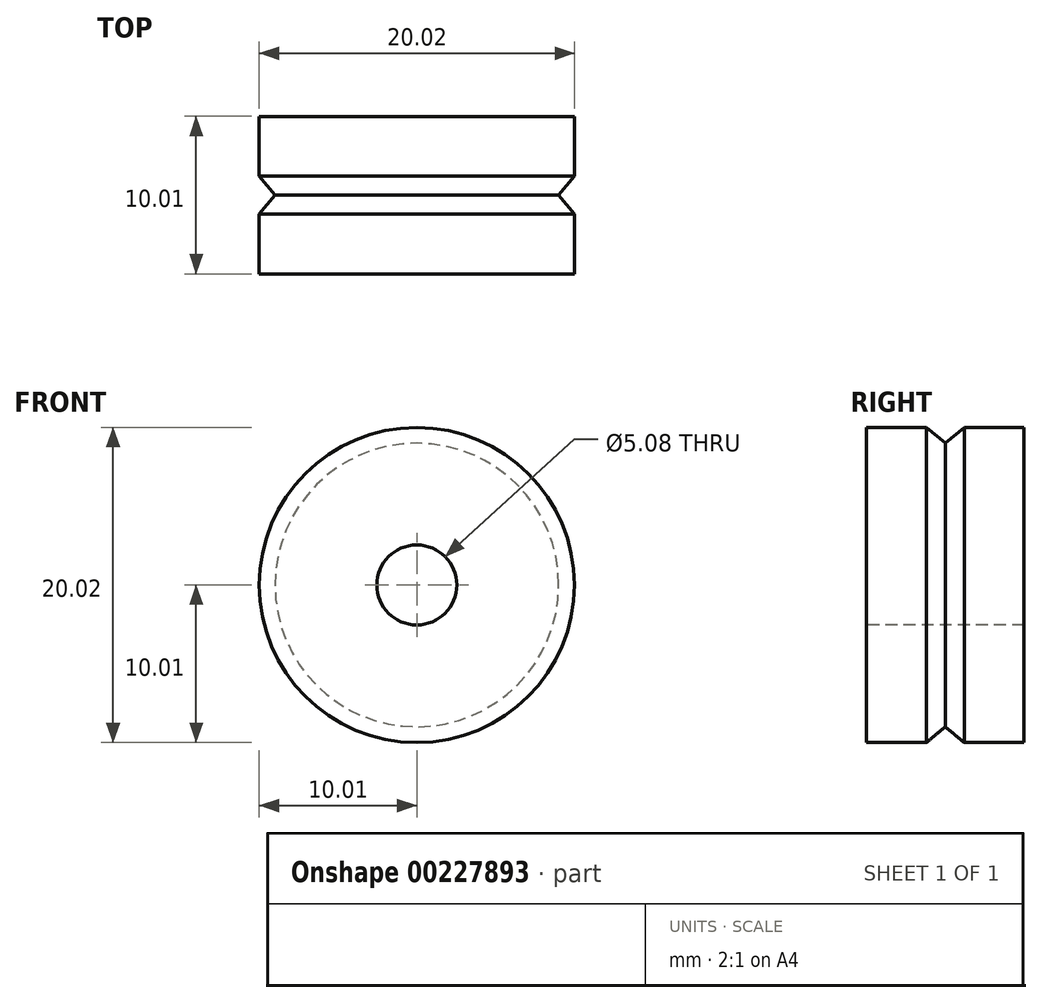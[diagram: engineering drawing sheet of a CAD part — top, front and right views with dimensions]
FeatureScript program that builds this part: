
annotation { "Feature Type Name" : "Feature", "Feature Type Description" : "" }
export const myFeature = defineFeature(function(context is Context, id is Id, definition is map)
    precondition{}
    {
        {
            var Q0;
            Q0=qCreatedBy(makeId("Right.planeOp"),FACE);
            var sketch = newSketch(context, id + "F0", { "sketchPlane" : qUnion([Q0])});
            skLineSegment(sketch, "E0", {"start": v(0, 10) * mm, "end": v(3.8, 10) * mm});
            skLineSegment(sketch, "E1", {"start": v(3.8, 10) * mm, "end": v(5, 9) * mm});
            skLineSegment(sketch, "E2", {"start": v(5, 9) * mm, "end": v(6.2, 10) * mm});
            skLineSegment(sketch, "E3", {"start": v(6.2, 10) * mm, "end": v(10, 10) * mm});
            skLineSegment(sketch, "E4", {"start": v(10, 10) * mm, "end": v(10, 0) * mm});
            skLineSegment(sketch, "E5", {"start": v(0, 0) * mm, "end": v(10, 0) * mm});
            skLineSegment(sketch, "E6", {"start": v(0, 10) * mm, "end": v(0, 0) * mm});
            skSolve(sketch);
        }
        {
            var Q0;
            Q0 = qSketchRegion(id + "F0", true);
            var Q1;
            Q1=sQuery(id+"F0.wireOp",EDGE,"E5");
            revolve(context, id + "F1", {"entities" : qUnion([Q0]), "axis" : qUnion([Q1]), "revolveType" : RevolveType.FULL});
        }
        {
            var Q0;
            Q0=makeQuery(id+"F1.opRevolve","SWEPT_FACE",FACE,{"disambiguationData":[OSD([sQuery(id+"F0.wireOp",EDGE,"E6")])]});
            var sketch = newSketch(context, id + "F2", { "sketchPlane" : qUnion([Q0])});
            skCircle(sketch, "E7", {"center": v(0, 0) * mm, "radius": 2.54 * mm});
            skSolve(sketch);
        }
        {
            var Q0;
            Q0 = qSketchRegion(id + "F2", true);
            extrude(context, id + "F3", {"entities" : qUnion([Q0]), "operationType" : NewBodyOperationType.REMOVE, "endBound" : BoundingType.UP_TO_NEXT, "oppositeDirection" : true, "depth" : 25.4 * mm});
        }
    });
